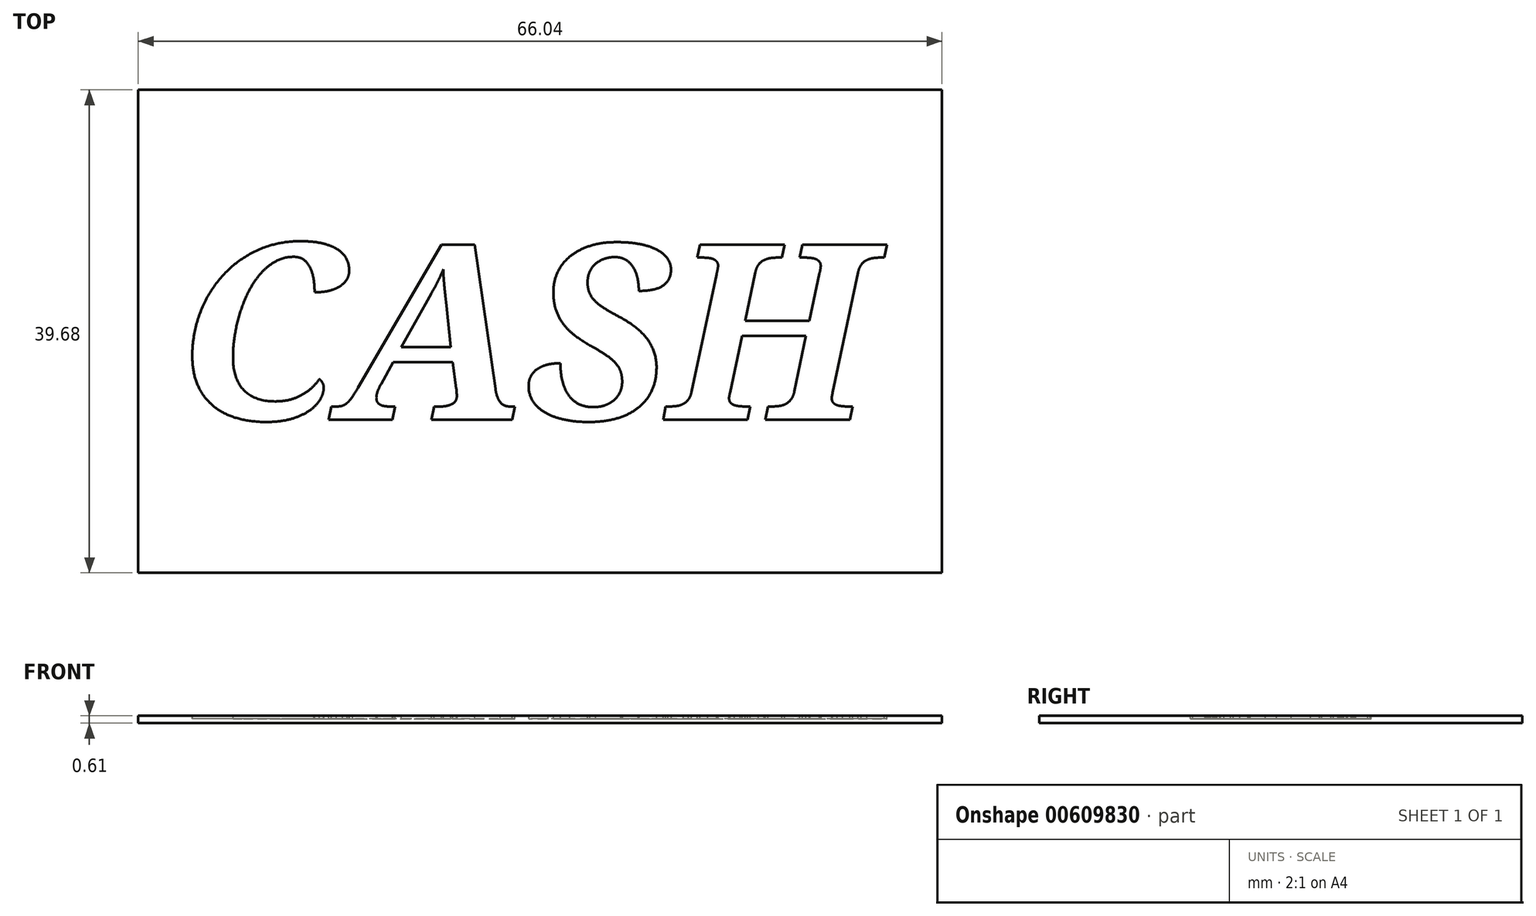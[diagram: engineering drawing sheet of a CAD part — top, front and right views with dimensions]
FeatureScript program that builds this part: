
annotation { "Feature Type Name" : "Feature", "Feature Type Description" : "" }
export const myFeature = defineFeature(function(context is Context, id is Id, definition is map)
    precondition{}
    {
        {
            var Q0;
            Q0=qCreatedBy(makeId("Top.planeOp"),FACE);
            var sketch = newSketch(context, id + "F0", { "sketchPlane" : qUnion([Q0])});
            skLineSegment(sketch, "E0.bottom", {"start": v(-33.02, 19.84) * mm, "end": v(33.02, 19.84) * mm});
            skLineSegment(sketch, "E0.top", {"start": v(-33.02, -19.84) * mm, "end": v(33.02, -19.84) * mm});
            skLineSegment(sketch, "E0.left", {"start": v(-33.02, 19.84) * mm, "end": v(-33.02, -19.84) * mm});
            skLineSegment(sketch, "E0.right", {"start": v(33.02, 19.84) * mm, "end": v(33.02, -19.84) * mm});
            skPoint(sketch, "E0.middle", {"position": v(0, 0) * mm});
            skSolve(sketch);
        }
        {
            var Q0;
            Q0 = qSketchRegion(id + "F0", true);
            extrude(context, id + "F1", {"entities" : qUnion([Q0]), "depth" : 0.6 * mm, "offsetDistance" : 25.4 * mm});
        }
        {
            var Q0;
            Q0=makeQuery(id+"F1.opExtrude","CAP_FACE",FACE,{"disambiguationData":[OSD([sQuery(id+"F0.wireOp",EDGE,"E0.bottom"),sQuery(id+"F0.wireOp",EDGE,"E0.top"),sQuery(id+"F0.wireOp",EDGE,"E0.left"),sQuery(id+"F0.wireOp",EDGE,"E0.right")])],"isStart":false});
            var sketch = newSketch(context, id + "F2", { "sketchPlane" : qUnion([Q0])});
            skText(sketch, "E1", { "text": "CASH", "fontName": "NotoSerif-BoldItalic.ttf"});
            skLineSegment(sketch, "E2", {"start": v(-29.85, 0) * mm, "end": v(-33.02, 0) * mm, "construction": true});
            skLineSegment(sketch, "E3", {"start": v(0, 7.25) * mm, "end": v(0, 19.84) * mm, "construction": true});
            const initialGuessF2  = {"E1": [-0.02985, -0.00725, 1, 0, 0.0145]};
            skSetInitialGuess(sketch, initialGuessF2);
            skSolve(sketch);
        }
        {
            var Q0;
            Q0 = qSketchRegion(id + "F2", true);
            extrude(context, id + "F3", {"entities" : qUnion([Q0]), "operationType" : NewBodyOperationType.REMOVE, "oppositeDirection" : true, "depth" : 0.25 * mm, "offsetDistance" : 25.4 * mm});
        }
    });
